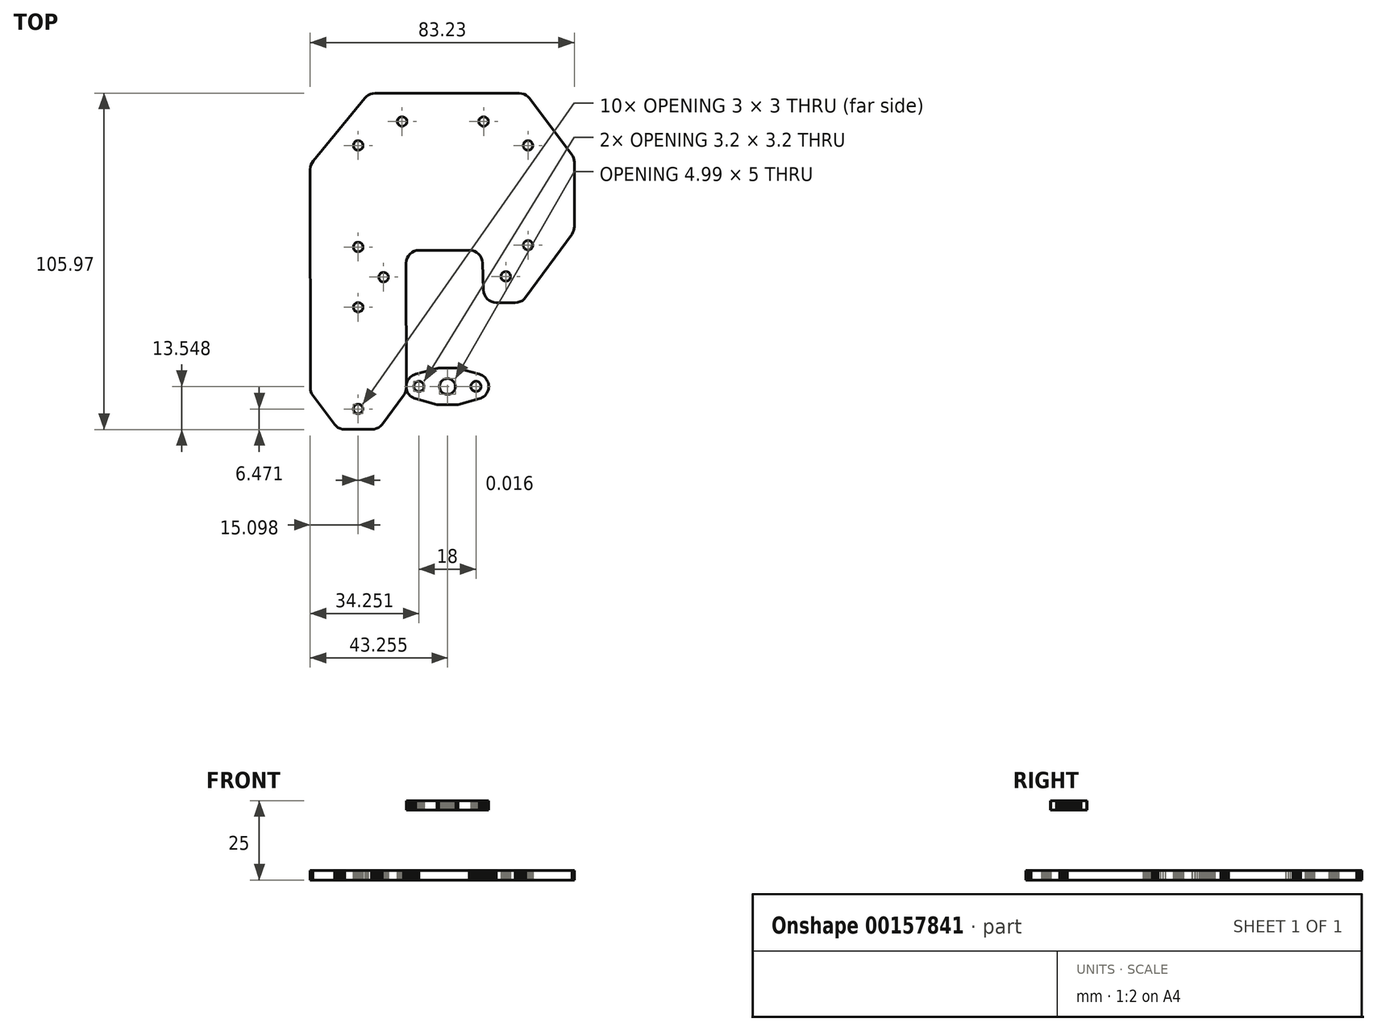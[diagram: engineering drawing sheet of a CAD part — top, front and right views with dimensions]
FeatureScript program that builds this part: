
annotation { "Feature Type Name" : "Feature", "Feature Type Description" : "" }
export const myFeature = defineFeature(function(context is Context, id is Id, definition is map)
    precondition{}
    {
        {
            var Q0;
            Q0=qCreatedBy(makeId("Top.planeOp"),FACE);
            var sketch = newSketch(context, id + "F0", { "sketchPlane" : qUnion([Q0])});
            skLineSegment(sketch, "E0", {"start": v(-52.7, 32.97) * mm, "end": v(-52.37, 33.65) * mm});
            skLineSegment(sketch, "E1", {"start": v(-52.91, 32.24) * mm, "end": v(-52.7, 32.97) * mm});
            skLineSegment(sketch, "E2", {"start": v(-52.98, 31.49) * mm, "end": v(-52.91, 32.24) * mm});
            skLineSegment(sketch, "E3", {"start": v(-52.98, -14.02) * mm, "end": v(-52.98, 31.49) * mm});
            skLineSegment(sketch, "E4", {"start": v(-52.92, -14.74) * mm, "end": v(-52.98, -14.02) * mm});
            skLineSegment(sketch, "E5", {"start": v(-52.73, -15.44) * mm, "end": v(-52.92, -14.74) * mm});
            skLineSegment(sketch, "E6", {"start": v(-52.42, -16.1) * mm, "end": v(-52.73, -15.44) * mm});
            skLineSegment(sketch, "E7", {"start": v(-52, -16.68) * mm, "end": v(-52.42, -16.1) * mm});
            skLineSegment(sketch, "E8", {"start": v(-51.48, -17.19) * mm, "end": v(-52, -16.68) * mm});
            skLineSegment(sketch, "E9", {"start": v(-31.6, -33.48) * mm, "end": v(-51.48, -17.19) * mm});
            skLineSegment(sketch, "E10", {"start": v(-31.03, -33.88) * mm, "end": v(-31.6, -33.48) * mm});
            skLineSegment(sketch, "E11", {"start": v(-30.39, -34.17) * mm, "end": v(-31.03, -33.88) * mm});
            skLineSegment(sketch, "E12", {"start": v(-29.7, -34.35) * mm, "end": v(-30.39, -34.17) * mm});
            skLineSegment(sketch, "E13", {"start": v(-29, -34.4) * mm, "end": v(-29.7, -34.35) * mm});
            skLineSegment(sketch, "E14", {"start": v(39.83, -34.37) * mm, "end": v(-29, -34.4) * mm});
            skLineSegment(sketch, "E15", {"start": v(40.48, -34.32) * mm, "end": v(39.83, -34.37) * mm});
            skLineSegment(sketch, "E16", {"start": v(41.12, -34.16) * mm, "end": v(40.48, -34.32) * mm});
            skLineSegment(sketch, "E17", {"start": v(41.73, -33.9) * mm, "end": v(41.12, -34.16) * mm});
            skLineSegment(sketch, "E18", {"start": v(42.28, -33.55) * mm, "end": v(41.73, -33.9) * mm});
            skLineSegment(sketch, "E19", {"start": v(51.35, -26.76) * mm, "end": v(42.28, -33.55) * mm});
            skLineSegment(sketch, "E20", {"start": v(51.9, -26.25) * mm, "end": v(51.35, -26.76) * mm});
            skLineSegment(sketch, "E21", {"start": v(52.37, -25.64) * mm, "end": v(51.9, -26.25) * mm});
            skLineSegment(sketch, "E22", {"start": v(52.7, -24.96) * mm, "end": v(52.37, -25.64) * mm});
            skLineSegment(sketch, "E23", {"start": v(52.91, -24.23) * mm, "end": v(52.7, -24.96) * mm});
            skLineSegment(sketch, "E24", {"start": v(52.98, -23.48) * mm, "end": v(52.91, -24.23) * mm});
            skLineSegment(sketch, "E25", {"start": v(52.98, -15.05) * mm, "end": v(52.98, -23.48) * mm});
            skLineSegment(sketch, "E26", {"start": v(52.9, -14.3) * mm, "end": v(52.98, -15.05) * mm});
            skLineSegment(sketch, "E27", {"start": v(52.7, -13.56) * mm, "end": v(52.9, -14.3) * mm});
            skLineSegment(sketch, "E28", {"start": v(52.36, -12.89) * mm, "end": v(52.7, -13.56) * mm});
            skLineSegment(sketch, "E29", {"start": v(51.9, -12.28) * mm, "end": v(52.36, -12.89) * mm});
            skLineSegment(sketch, "E30", {"start": v(51.34, -11.77) * mm, "end": v(51.9, -12.28) * mm});
            skLineSegment(sketch, "E31", {"start": v(42.28, -4.98) * mm, "end": v(51.34, -11.77) * mm});
            skLineSegment(sketch, "E32", {"start": v(41.72, -4.63) * mm, "end": v(42.28, -4.98) * mm});
            skLineSegment(sketch, "E33", {"start": v(41.11, -4.37) * mm, "end": v(41.72, -4.63) * mm});
            skLineSegment(sketch, "E34", {"start": v(40.47, -4.21) * mm, "end": v(41.11, -4.37) * mm});
            skLineSegment(sketch, "E35", {"start": v(39.82, -4.16) * mm, "end": v(40.47, -4.21) * mm});
            skLineSegment(sketch, "E36", {"start": v(0.57, -4.2) * mm, "end": v(39.82, -4.16) * mm});
            skLineSegment(sketch, "E37", {"start": v(-0.23, -4.11) * mm, "end": v(0.57, -4.2) * mm});
            skLineSegment(sketch, "E38", {"start": v(-1, -3.88) * mm, "end": v(-0.23, -4.11) * mm});
            skLineSegment(sketch, "E39", {"start": v(-1.7, -3.5) * mm, "end": v(-1, -3.88) * mm});
            skLineSegment(sketch, "E40", {"start": v(-2.33, -3) * mm, "end": v(-1.7, -3.5) * mm});
            skLineSegment(sketch, "E41", {"start": v(-2.84, -2.37) * mm, "end": v(-2.33, -3) * mm});
            skLineSegment(sketch, "E42", {"start": v(-3.22, -1.66) * mm, "end": v(-2.84, -2.37) * mm});
            skLineSegment(sketch, "E43", {"start": v(-3.45, -0.9) * mm, "end": v(-3.22, -1.66) * mm});
            skLineSegment(sketch, "E44", {"start": v(-3.53, -0.1) * mm, "end": v(-3.45, -0.9) * mm});
            skLineSegment(sketch, "E45", {"start": v(-3.53, 15.77) * mm, "end": v(-3.53, -0.1) * mm});
            skLineSegment(sketch, "E46", {"start": v(-3.45, 16.55) * mm, "end": v(-3.53, 15.77) * mm});
            skLineSegment(sketch, "E47", {"start": v(-3.23, 17.3) * mm, "end": v(-3.45, 16.55) * mm});
            skLineSegment(sketch, "E48", {"start": v(-2.87, 18) * mm, "end": v(-3.23, 17.3) * mm});
            skLineSegment(sketch, "E49", {"start": v(-2.37, 18.62) * mm, "end": v(-2.87, 18) * mm});
            skLineSegment(sketch, "E50", {"start": v(-1.78, 19.13) * mm, "end": v(-2.37, 18.62) * mm});
            skLineSegment(sketch, "E51", {"start": v(-1.1, 19.52) * mm, "end": v(-1.78, 19.13) * mm});
            skLineSegment(sketch, "E52", {"start": v(-0.34, 19.76) * mm, "end": v(-1.1, 19.52) * mm});
            skLineSegment(sketch, "E53", {"start": v(0.44, 19.86) * mm, "end": v(-0.34, 19.76) * mm});
            skLineSegment(sketch, "E54", {"start": v(9.04, 20.14) * mm, "end": v(0.44, 19.86) * mm});
            skLineSegment(sketch, "E55", {"start": v(9.82, 20.24) * mm, "end": v(9.04, 20.14) * mm});
            skLineSegment(sketch, "E56", {"start": v(10.57, 20.48) * mm, "end": v(9.82, 20.24) * mm});
            skLineSegment(sketch, "E57", {"start": v(11.25, 20.87) * mm, "end": v(10.57, 20.48) * mm});
            skLineSegment(sketch, "E58", {"start": v(11.85, 21.38) * mm, "end": v(11.25, 20.87) * mm});
            skLineSegment(sketch, "E59", {"start": v(12.34, 22) * mm, "end": v(11.85, 21.38) * mm});
            skLineSegment(sketch, "E60", {"start": v(12.7, 22.7) * mm, "end": v(12.34, 22) * mm});
            skLineSegment(sketch, "E61", {"start": v(12.93, 23.45) * mm, "end": v(12.7, 22.7) * mm});
            skLineSegment(sketch, "E62", {"start": v(13, 24.23) * mm, "end": v(12.93, 23.45) * mm});
            skLineSegment(sketch, "E63", {"start": v(13, 30.23) * mm, "end": v(13, 24.23) * mm});
            skLineSegment(sketch, "E64", {"start": v(12.93, 31) * mm, "end": v(13, 30.23) * mm});
            skLineSegment(sketch, "E65", {"start": v(12.72, 31.73) * mm, "end": v(12.93, 31) * mm});
            skLineSegment(sketch, "E66", {"start": v(12.37, 32.42) * mm, "end": v(12.72, 31.73) * mm});
            skLineSegment(sketch, "E67", {"start": v(11.9, 33.03) * mm, "end": v(12.37, 32.42) * mm});
            skLineSegment(sketch, "E68", {"start": v(11.32, 33.54) * mm, "end": v(11.9, 33.03) * mm});
            skLineSegment(sketch, "E69", {"start": v(-8.58, 48.04) * mm, "end": v(11.32, 33.54) * mm});
            skLineSegment(sketch, "E70", {"start": v(-9.13, 48.38) * mm, "end": v(-8.58, 48.04) * mm});
            skLineSegment(sketch, "E71", {"start": v(-9.72, 48.63) * mm, "end": v(-9.13, 48.38) * mm});
            skLineSegment(sketch, "E72", {"start": v(-10.35, 48.78) * mm, "end": v(-9.72, 48.63) * mm});
            skLineSegment(sketch, "E73", {"start": v(-11, 48.83) * mm, "end": v(-10.35, 48.78) * mm});
            skLineSegment(sketch, "E74", {"start": v(-31.23, 48.83) * mm, "end": v(-11, 48.83) * mm});
            skLineSegment(sketch, "E75", {"start": v(-31.88, 48.77) * mm, "end": v(-31.23, 48.83) * mm});
            skLineSegment(sketch, "E76", {"start": v(-32.52, 48.62) * mm, "end": v(-31.88, 48.77) * mm});
            skLineSegment(sketch, "E77", {"start": v(-33.13, 48.36) * mm, "end": v(-32.52, 48.62) * mm});
            skLineSegment(sketch, "E78", {"start": v(-33.68, 48) * mm, "end": v(-33.13, 48.36) * mm});
            skLineSegment(sketch, "E79", {"start": v(-51.35, 34.76) * mm, "end": v(-33.68, 48) * mm});
            skLineSegment(sketch, "E80", {"start": v(-51.9, 34.25) * mm, "end": v(-51.35, 34.76) * mm});
            skLineSegment(sketch, "E81", {"start": v(-52.37, 33.65) * mm, "end": v(-51.9, 34.25) * mm});
            skLineSegment(sketch, "E82", {"start": v(-37.28, -18) * mm, "end": v(-37.6, -18.23) * mm});
            skLineSegment(sketch, "E83", {"start": v(-36.92, -17.84) * mm, "end": v(-37.28, -18) * mm});
            skLineSegment(sketch, "E84", {"start": v(-36.53, -17.8) * mm, "end": v(-36.92, -17.84) * mm});
            skLineSegment(sketch, "E85", {"start": v(-36.14, -17.84) * mm, "end": v(-36.53, -17.8) * mm});
            skLineSegment(sketch, "E86", {"start": v(-35.78, -18) * mm, "end": v(-36.14, -17.84) * mm});
            skLineSegment(sketch, "E87", {"start": v(-35.47, -18.23) * mm, "end": v(-35.78, -18) * mm});
            skLineSegment(sketch, "E88", {"start": v(-35.23, -18.54) * mm, "end": v(-35.47, -18.23) * mm});
            skLineSegment(sketch, "E89", {"start": v(-35.08, -18.9) * mm, "end": v(-35.23, -18.54) * mm});
            skLineSegment(sketch, "E90", {"start": v(-35.03, -19.3) * mm, "end": v(-35.08, -18.9) * mm});
            skLineSegment(sketch, "E91", {"start": v(-35.08, -19.68) * mm, "end": v(-35.03, -19.3) * mm});
            skLineSegment(sketch, "E92", {"start": v(-35.23, -20.04) * mm, "end": v(-35.08, -19.68) * mm});
            skLineSegment(sketch, "E93", {"start": v(-35.47, -20.35) * mm, "end": v(-35.23, -20.04) * mm});
            skLineSegment(sketch, "E94", {"start": v(-35.78, -20.6) * mm, "end": v(-35.47, -20.35) * mm});
            skLineSegment(sketch, "E95", {"start": v(-36.14, -20.74) * mm, "end": v(-35.78, -20.6) * mm});
            skLineSegment(sketch, "E96", {"start": v(-36.53, -20.8) * mm, "end": v(-36.14, -20.74) * mm});
            skLineSegment(sketch, "E97", {"start": v(-36.92, -20.74) * mm, "end": v(-36.53, -20.8) * mm});
            skLineSegment(sketch, "E98", {"start": v(-37.28, -20.6) * mm, "end": v(-36.92, -20.74) * mm});
            skLineSegment(sketch, "E99", {"start": v(-37.6, -20.35) * mm, "end": v(-37.28, -20.6) * mm});
            skLineSegment(sketch, "E100", {"start": v(-37.83, -20.04) * mm, "end": v(-37.6, -20.35) * mm});
            skLineSegment(sketch, "E101", {"start": v(-37.98, -19.68) * mm, "end": v(-37.83, -20.04) * mm});
            skLineSegment(sketch, "E102", {"start": v(-38.03, -19.3) * mm, "end": v(-37.98, -19.68) * mm});
            skLineSegment(sketch, "E103", {"start": v(-37.98, -18.9) * mm, "end": v(-38.03, -19.3) * mm});
            skLineSegment(sketch, "E104", {"start": v(-37.83, -18.54) * mm, "end": v(-37.98, -18.9) * mm});
            skLineSegment(sketch, "E105", {"start": v(-37.6, -18.23) * mm, "end": v(-37.83, -18.54) * mm});
            skLineSegment(sketch, "E106", {"start": v(-43.7, 21.68) * mm, "end": v(-44.09, 21.73) * mm});
            skLineSegment(sketch, "E107", {"start": v(-43.34, 21.53) * mm, "end": v(-43.7, 21.68) * mm});
            skLineSegment(sketch, "E108", {"start": v(-43.03, 21.3) * mm, "end": v(-43.34, 21.53) * mm});
            skLineSegment(sketch, "E109", {"start": v(-42.8, 20.98) * mm, "end": v(-43.03, 21.3) * mm});
            skLineSegment(sketch, "E110", {"start": v(-42.64, 20.62) * mm, "end": v(-42.8, 20.98) * mm});
            skLineSegment(sketch, "E111", {"start": v(-42.59, 20.23) * mm, "end": v(-42.64, 20.62) * mm});
            skLineSegment(sketch, "E112", {"start": v(-42.64, 19.84) * mm, "end": v(-42.59, 20.23) * mm});
            skLineSegment(sketch, "E113", {"start": v(-42.8, 19.48) * mm, "end": v(-42.64, 19.84) * mm});
            skLineSegment(sketch, "E114", {"start": v(-43.03, 19.17) * mm, "end": v(-42.8, 19.48) * mm});
            skLineSegment(sketch, "E115", {"start": v(-43.34, 18.93) * mm, "end": v(-43.03, 19.17) * mm});
            skLineSegment(sketch, "E116", {"start": v(-43.7, 18.78) * mm, "end": v(-43.34, 18.93) * mm});
            skLineSegment(sketch, "E117", {"start": v(-44.09, 18.73) * mm, "end": v(-43.7, 18.78) * mm});
            skLineSegment(sketch, "E118", {"start": v(-44.48, 18.78) * mm, "end": v(-44.09, 18.73) * mm});
            skLineSegment(sketch, "E119", {"start": v(-44.84, 18.93) * mm, "end": v(-44.48, 18.78) * mm});
            skLineSegment(sketch, "E120", {"start": v(-45.15, 19.17) * mm, "end": v(-44.84, 18.93) * mm});
            skLineSegment(sketch, "E121", {"start": v(-45.39, 19.48) * mm, "end": v(-45.15, 19.17) * mm});
            skLineSegment(sketch, "E122", {"start": v(-45.54, 19.84) * mm, "end": v(-45.39, 19.48) * mm});
            skLineSegment(sketch, "E123", {"start": v(-45.59, 20.23) * mm, "end": v(-45.54, 19.84) * mm});
            skLineSegment(sketch, "E124", {"start": v(-45.54, 20.62) * mm, "end": v(-45.59, 20.23) * mm});
            skLineSegment(sketch, "E125", {"start": v(-45.39, 20.98) * mm, "end": v(-45.54, 20.62) * mm});
            skLineSegment(sketch, "E126", {"start": v(-45.15, 21.3) * mm, "end": v(-45.39, 20.98) * mm});
            skLineSegment(sketch, "E127", {"start": v(-44.84, 21.53) * mm, "end": v(-45.15, 21.3) * mm});
            skLineSegment(sketch, "E128", {"start": v(-44.48, 21.68) * mm, "end": v(-44.84, 21.53) * mm});
            skLineSegment(sketch, "E129", {"start": v(-44.09, 21.73) * mm, "end": v(-44.48, 21.68) * mm});
            skLineSegment(sketch, "E130", {"start": v(-44.09, -6.96) * mm, "end": v(-43.7, -6.9) * mm});
            skLineSegment(sketch, "E131", {"start": v(-44.48, -6.9) * mm, "end": v(-44.09, -6.96) * mm});
            skLineSegment(sketch, "E132", {"start": v(-44.84, -6.76) * mm, "end": v(-44.48, -6.9) * mm});
            skLineSegment(sketch, "E133", {"start": v(-45.15, -6.52) * mm, "end": v(-44.84, -6.76) * mm});
            skLineSegment(sketch, "E134", {"start": v(-45.39, -6.21) * mm, "end": v(-45.15, -6.52) * mm});
            skLineSegment(sketch, "E135", {"start": v(-45.54, -5.85) * mm, "end": v(-45.39, -6.21) * mm});
            skLineSegment(sketch, "E136", {"start": v(-45.59, -5.46) * mm, "end": v(-45.54, -5.85) * mm});
            skLineSegment(sketch, "E137", {"start": v(-45.54, -5.07) * mm, "end": v(-45.59, -5.46) * mm});
            skLineSegment(sketch, "E138", {"start": v(-45.39, -4.71) * mm, "end": v(-45.54, -5.07) * mm});
            skLineSegment(sketch, "E139", {"start": v(-45.15, -4.4) * mm, "end": v(-45.39, -4.71) * mm});
            skLineSegment(sketch, "E140", {"start": v(-44.84, -4.16) * mm, "end": v(-45.15, -4.4) * mm});
            skLineSegment(sketch, "E141", {"start": v(-44.48, -4.01) * mm, "end": v(-44.84, -4.16) * mm});
            skLineSegment(sketch, "E142", {"start": v(-44.09, -3.96) * mm, "end": v(-44.48, -4.01) * mm});
            skLineSegment(sketch, "E143", {"start": v(-43.7, -4.01) * mm, "end": v(-44.09, -3.96) * mm});
            skLineSegment(sketch, "E144", {"start": v(-43.34, -4.16) * mm, "end": v(-43.7, -4.01) * mm});
            skLineSegment(sketch, "E145", {"start": v(-43.03, -4.4) * mm, "end": v(-43.34, -4.16) * mm});
            skLineSegment(sketch, "E146", {"start": v(-42.8, -4.71) * mm, "end": v(-43.03, -4.4) * mm});
            skLineSegment(sketch, "E147", {"start": v(-42.64, -5.07) * mm, "end": v(-42.8, -4.71) * mm});
            skLineSegment(sketch, "E148", {"start": v(-42.59, -5.46) * mm, "end": v(-42.64, -5.07) * mm});
            skLineSegment(sketch, "E149", {"start": v(-42.64, -5.85) * mm, "end": v(-42.59, -5.46) * mm});
            skLineSegment(sketch, "E150", {"start": v(-42.8, -6.21) * mm, "end": v(-42.64, -5.85) * mm});
            skLineSegment(sketch, "E151", {"start": v(-43.03, -6.52) * mm, "end": v(-42.8, -6.21) * mm});
            skLineSegment(sketch, "E152", {"start": v(-43.34, -6.76) * mm, "end": v(-43.03, -6.52) * mm});
            skLineSegment(sketch, "E153", {"start": v(-43.7, -6.9) * mm, "end": v(-43.34, -6.76) * mm});
            skLineSegment(sketch, "E154", {"start": v(-35.47, 33.17) * mm, "end": v(-35.23, 33.48) * mm});
            skLineSegment(sketch, "E155", {"start": v(-35.78, 32.93) * mm, "end": v(-35.47, 33.17) * mm});
            skLineSegment(sketch, "E156", {"start": v(-36.14, 32.78) * mm, "end": v(-35.78, 32.93) * mm});
            skLineSegment(sketch, "E157", {"start": v(-36.53, 32.73) * mm, "end": v(-36.14, 32.78) * mm});
            skLineSegment(sketch, "E158", {"start": v(-36.92, 32.78) * mm, "end": v(-36.53, 32.73) * mm});
            skLineSegment(sketch, "E159", {"start": v(-37.28, 32.93) * mm, "end": v(-36.92, 32.78) * mm});
            skLineSegment(sketch, "E160", {"start": v(-37.6, 33.17) * mm, "end": v(-37.28, 32.93) * mm});
            skLineSegment(sketch, "E161", {"start": v(-37.83, 33.48) * mm, "end": v(-37.6, 33.17) * mm});
            skLineSegment(sketch, "E162", {"start": v(-37.98, 33.84) * mm, "end": v(-37.83, 33.48) * mm});
            skLineSegment(sketch, "E163", {"start": v(-38.03, 34.23) * mm, "end": v(-37.98, 33.84) * mm});
            skLineSegment(sketch, "E164", {"start": v(-37.98, 34.62) * mm, "end": v(-38.03, 34.23) * mm});
            skLineSegment(sketch, "E165", {"start": v(-37.83, 34.98) * mm, "end": v(-37.98, 34.62) * mm});
            skLineSegment(sketch, "E166", {"start": v(-37.6, 35.3) * mm, "end": v(-37.83, 34.98) * mm});
            skLineSegment(sketch, "E167", {"start": v(-37.28, 35.53) * mm, "end": v(-37.6, 35.3) * mm});
            skLineSegment(sketch, "E168", {"start": v(-36.92, 35.68) * mm, "end": v(-37.28, 35.53) * mm});
            skLineSegment(sketch, "E169", {"start": v(-36.53, 35.73) * mm, "end": v(-36.92, 35.68) * mm});
            skLineSegment(sketch, "E170", {"start": v(-36.14, 35.68) * mm, "end": v(-36.53, 35.73) * mm});
            skLineSegment(sketch, "E171", {"start": v(-35.78, 35.53) * mm, "end": v(-36.14, 35.68) * mm});
            skLineSegment(sketch, "E172", {"start": v(-35.47, 35.3) * mm, "end": v(-35.78, 35.53) * mm});
            skLineSegment(sketch, "E173", {"start": v(-35.23, 34.98) * mm, "end": v(-35.47, 35.3) * mm});
            skLineSegment(sketch, "E174", {"start": v(-35.08, 34.62) * mm, "end": v(-35.23, 34.98) * mm});
            skLineSegment(sketch, "E175", {"start": v(-35.03, 34.23) * mm, "end": v(-35.08, 34.62) * mm});
            skLineSegment(sketch, "E176", {"start": v(-35.08, 33.84) * mm, "end": v(-35.03, 34.23) * mm});
            skLineSegment(sketch, "E177", {"start": v(-35.23, 33.48) * mm, "end": v(-35.08, 33.84) * mm});
            skLineSegment(sketch, "E178", {"start": v(-5.09, 32.73) * mm, "end": v(-4.7, 32.78) * mm});
            skLineSegment(sketch, "E179", {"start": v(-5.48, 32.78) * mm, "end": v(-5.09, 32.73) * mm});
            skLineSegment(sketch, "E180", {"start": v(-5.84, 32.93) * mm, "end": v(-5.48, 32.78) * mm});
            skLineSegment(sketch, "E181", {"start": v(-6.15, 33.17) * mm, "end": v(-5.84, 32.93) * mm});
            skLineSegment(sketch, "E182", {"start": v(-6.39, 33.48) * mm, "end": v(-6.15, 33.17) * mm});
            skLineSegment(sketch, "E183", {"start": v(-6.54, 33.84) * mm, "end": v(-6.39, 33.48) * mm});
            skLineSegment(sketch, "E184", {"start": v(-6.59, 34.23) * mm, "end": v(-6.54, 33.84) * mm});
            skLineSegment(sketch, "E185", {"start": v(-6.54, 34.62) * mm, "end": v(-6.59, 34.23) * mm});
            skLineSegment(sketch, "E186", {"start": v(-6.39, 34.98) * mm, "end": v(-6.54, 34.62) * mm});
            skLineSegment(sketch, "E187", {"start": v(-6.15, 35.3) * mm, "end": v(-6.39, 34.98) * mm});
            skLineSegment(sketch, "E188", {"start": v(-5.84, 35.53) * mm, "end": v(-6.15, 35.3) * mm});
            skLineSegment(sketch, "E189", {"start": v(-5.48, 35.68) * mm, "end": v(-5.84, 35.53) * mm});
            skLineSegment(sketch, "E190", {"start": v(-5.09, 35.73) * mm, "end": v(-5.48, 35.68) * mm});
            skLineSegment(sketch, "E191", {"start": v(-4.7, 35.68) * mm, "end": v(-5.09, 35.73) * mm});
            skLineSegment(sketch, "E192", {"start": v(-4.34, 35.53) * mm, "end": v(-4.7, 35.68) * mm});
            skLineSegment(sketch, "E193", {"start": v(-4.03, 35.3) * mm, "end": v(-4.34, 35.53) * mm});
            skLineSegment(sketch, "E194", {"start": v(-3.8, 34.98) * mm, "end": v(-4.03, 35.3) * mm});
            skLineSegment(sketch, "E195", {"start": v(-3.64, 34.62) * mm, "end": v(-3.8, 34.98) * mm});
            skLineSegment(sketch, "E196", {"start": v(-3.59, 34.23) * mm, "end": v(-3.64, 34.62) * mm});
            skLineSegment(sketch, "E197", {"start": v(-3.64, 33.84) * mm, "end": v(-3.59, 34.23) * mm});
            skLineSegment(sketch, "E198", {"start": v(-3.8, 33.48) * mm, "end": v(-3.64, 33.84) * mm});
            skLineSegment(sketch, "E199", {"start": v(-4.03, 33.17) * mm, "end": v(-3.8, 33.48) * mm});
            skLineSegment(sketch, "E200", {"start": v(-4.34, 32.93) * mm, "end": v(-4.03, 33.17) * mm});
            skLineSegment(sketch, "E201", {"start": v(-4.7, 32.78) * mm, "end": v(-4.34, 32.93) * mm});
            skLineSegment(sketch, "E202", {"start": v(4.74, 25.73) * mm, "end": v(5.13, 25.78) * mm});
            skLineSegment(sketch, "E203", {"start": v(4.35, 25.78) * mm, "end": v(4.74, 25.73) * mm});
            skLineSegment(sketch, "E204", {"start": v(3.99, 25.93) * mm, "end": v(4.35, 25.78) * mm});
            skLineSegment(sketch, "E205", {"start": v(3.68, 26.17) * mm, "end": v(3.99, 25.93) * mm});
            skLineSegment(sketch, "E206", {"start": v(3.44, 26.48) * mm, "end": v(3.68, 26.17) * mm});
            skLineSegment(sketch, "E207", {"start": v(3.29, 26.84) * mm, "end": v(3.44, 26.48) * mm});
            skLineSegment(sketch, "E208", {"start": v(3.24, 27.23) * mm, "end": v(3.29, 26.84) * mm});
            skLineSegment(sketch, "E209", {"start": v(3.29, 27.62) * mm, "end": v(3.24, 27.23) * mm});
            skLineSegment(sketch, "E210", {"start": v(3.44, 27.98) * mm, "end": v(3.29, 27.62) * mm});
            skLineSegment(sketch, "E211", {"start": v(3.68, 28.3) * mm, "end": v(3.44, 27.98) * mm});
            skLineSegment(sketch, "E212", {"start": v(3.99, 28.53) * mm, "end": v(3.68, 28.3) * mm});
            skLineSegment(sketch, "E213", {"start": v(4.35, 28.68) * mm, "end": v(3.99, 28.53) * mm});
            skLineSegment(sketch, "E214", {"start": v(4.74, 28.73) * mm, "end": v(4.35, 28.68) * mm});
            skLineSegment(sketch, "E215", {"start": v(5.13, 28.68) * mm, "end": v(4.74, 28.73) * mm});
            skLineSegment(sketch, "E216", {"start": v(5.49, 28.53) * mm, "end": v(5.13, 28.68) * mm});
            skLineSegment(sketch, "E217", {"start": v(5.8, 28.3) * mm, "end": v(5.49, 28.53) * mm});
            skLineSegment(sketch, "E218", {"start": v(6.04, 27.98) * mm, "end": v(5.8, 28.3) * mm});
            skLineSegment(sketch, "E219", {"start": v(6.19, 27.62) * mm, "end": v(6.04, 27.98) * mm});
            skLineSegment(sketch, "E220", {"start": v(6.24, 27.23) * mm, "end": v(6.19, 27.62) * mm});
            skLineSegment(sketch, "E221", {"start": v(6.19, 26.84) * mm, "end": v(6.24, 27.23) * mm});
            skLineSegment(sketch, "E222", {"start": v(6.04, 26.48) * mm, "end": v(6.19, 26.84) * mm});
            skLineSegment(sketch, "E223", {"start": v(5.8, 26.17) * mm, "end": v(6.04, 26.48) * mm});
            skLineSegment(sketch, "E224", {"start": v(5.49, 25.93) * mm, "end": v(5.8, 26.17) * mm});
            skLineSegment(sketch, "E225", {"start": v(5.13, 25.78) * mm, "end": v(5.49, 25.93) * mm});
            skLineSegment(sketch, "E226", {"start": v(3.53, -10.9) * mm, "end": v(3.47, -11.29) * mm});
            skLineSegment(sketch, "E227", {"start": v(3.68, -10.54) * mm, "end": v(3.53, -10.9) * mm});
            skLineSegment(sketch, "E228", {"start": v(3.91, -10.23) * mm, "end": v(3.68, -10.54) * mm});
            skLineSegment(sketch, "E229", {"start": v(4.22, -9.99) * mm, "end": v(3.91, -10.23) * mm});
            skLineSegment(sketch, "E230", {"start": v(4.59, -9.84) * mm, "end": v(4.22, -9.99) * mm});
            skLineSegment(sketch, "E231", {"start": v(4.97, -9.79) * mm, "end": v(4.59, -9.84) * mm});
            skLineSegment(sketch, "E232", {"start": v(5.36, -9.84) * mm, "end": v(4.97, -9.79) * mm});
            skLineSegment(sketch, "E233", {"start": v(5.72, -9.99) * mm, "end": v(5.36, -9.84) * mm});
            skLineSegment(sketch, "E234", {"start": v(6.04, -10.23) * mm, "end": v(5.72, -9.99) * mm});
            skLineSegment(sketch, "E235", {"start": v(6.27, -10.54) * mm, "end": v(6.04, -10.23) * mm});
            skLineSegment(sketch, "E236", {"start": v(6.42, -10.9) * mm, "end": v(6.27, -10.54) * mm});
            skLineSegment(sketch, "E237", {"start": v(6.47, -11.29) * mm, "end": v(6.42, -10.9) * mm});
            skLineSegment(sketch, "E238", {"start": v(6.42, -11.68) * mm, "end": v(6.47, -11.29) * mm});
            skLineSegment(sketch, "E239", {"start": v(6.27, -12.04) * mm, "end": v(6.42, -11.68) * mm});
            skLineSegment(sketch, "E240", {"start": v(6.04, -12.35) * mm, "end": v(6.27, -12.04) * mm});
            skLineSegment(sketch, "E241", {"start": v(5.72, -12.59) * mm, "end": v(6.04, -12.35) * mm});
            skLineSegment(sketch, "E242", {"start": v(5.36, -12.74) * mm, "end": v(5.72, -12.59) * mm});
            skLineSegment(sketch, "E243", {"start": v(4.97, -12.79) * mm, "end": v(5.36, -12.74) * mm});
            skLineSegment(sketch, "E244", {"start": v(4.59, -12.74) * mm, "end": v(4.97, -12.79) * mm});
            skLineSegment(sketch, "E245", {"start": v(4.22, -12.59) * mm, "end": v(4.59, -12.74) * mm});
            skLineSegment(sketch, "E246", {"start": v(3.91, -12.35) * mm, "end": v(4.22, -12.59) * mm});
            skLineSegment(sketch, "E247", {"start": v(3.68, -12.04) * mm, "end": v(3.91, -12.35) * mm});
            skLineSegment(sketch, "E248", {"start": v(3.53, -11.68) * mm, "end": v(3.68, -12.04) * mm});
            skLineSegment(sketch, "E249", {"start": v(3.47, -11.29) * mm, "end": v(3.53, -11.68) * mm});
            skLineSegment(sketch, "E250", {"start": v(-4.91, -20.74) * mm, "end": v(-4.53, -20.8) * mm});
            skLineSegment(sketch, "E251", {"start": v(-5.28, -20.6) * mm, "end": v(-4.91, -20.74) * mm});
            skLineSegment(sketch, "E252", {"start": v(-5.59, -20.35) * mm, "end": v(-5.28, -20.6) * mm});
            skLineSegment(sketch, "E253", {"start": v(-5.82, -20.04) * mm, "end": v(-5.59, -20.35) * mm});
            skLineSegment(sketch, "E254", {"start": v(-5.97, -19.68) * mm, "end": v(-5.82, -20.04) * mm});
            skLineSegment(sketch, "E255", {"start": v(-6.03, -19.3) * mm, "end": v(-5.97, -19.68) * mm});
            skLineSegment(sketch, "E256", {"start": v(-5.97, -18.9) * mm, "end": v(-6.03, -19.3) * mm});
            skLineSegment(sketch, "E257", {"start": v(-5.82, -18.54) * mm, "end": v(-5.97, -18.9) * mm});
            skLineSegment(sketch, "E258", {"start": v(-5.59, -18.23) * mm, "end": v(-5.82, -18.54) * mm});
            skLineSegment(sketch, "E259", {"start": v(-5.28, -18) * mm, "end": v(-5.59, -18.23) * mm});
            skLineSegment(sketch, "E260", {"start": v(-4.91, -17.84) * mm, "end": v(-5.28, -18) * mm});
            skLineSegment(sketch, "E261", {"start": v(-4.53, -17.8) * mm, "end": v(-4.91, -17.84) * mm});
            skLineSegment(sketch, "E262", {"start": v(-4.14, -17.84) * mm, "end": v(-4.53, -17.8) * mm});
            skLineSegment(sketch, "E263", {"start": v(-3.78, -18) * mm, "end": v(-4.14, -17.84) * mm});
            skLineSegment(sketch, "E264", {"start": v(-3.46, -18.23) * mm, "end": v(-3.78, -18) * mm});
            skLineSegment(sketch, "E265", {"start": v(-3.23, -18.54) * mm, "end": v(-3.46, -18.23) * mm});
            skLineSegment(sketch, "E266", {"start": v(-3.08, -18.9) * mm, "end": v(-3.23, -18.54) * mm});
            skLineSegment(sketch, "E267", {"start": v(-3.03, -19.3) * mm, "end": v(-3.08, -18.9) * mm});
            skLineSegment(sketch, "E268", {"start": v(-3.08, -19.68) * mm, "end": v(-3.03, -19.3) * mm});
            skLineSegment(sketch, "E269", {"start": v(-3.23, -20.04) * mm, "end": v(-3.08, -19.68) * mm});
            skLineSegment(sketch, "E270", {"start": v(-3.46, -20.35) * mm, "end": v(-3.23, -20.04) * mm});
            skLineSegment(sketch, "E271", {"start": v(-3.78, -20.6) * mm, "end": v(-3.46, -20.35) * mm});
            skLineSegment(sketch, "E272", {"start": v(-4.14, -20.74) * mm, "end": v(-3.78, -20.6) * mm});
            skLineSegment(sketch, "E273", {"start": v(-4.53, -20.8) * mm, "end": v(-4.14, -20.74) * mm});
            skLineSegment(sketch, "E274", {"start": v(15.54, -20.34) * mm, "end": v(15.77, -20.03) * mm});
            skLineSegment(sketch, "E275", {"start": v(15.22, -20.58) * mm, "end": v(15.54, -20.34) * mm});
            skLineSegment(sketch, "E276", {"start": v(14.86, -20.73) * mm, "end": v(15.22, -20.58) * mm});
            skLineSegment(sketch, "E277", {"start": v(14.47, -20.78) * mm, "end": v(14.86, -20.73) * mm});
            skLineSegment(sketch, "E278", {"start": v(14.09, -20.73) * mm, "end": v(14.47, -20.78) * mm});
            skLineSegment(sketch, "E279", {"start": v(13.72, -20.58) * mm, "end": v(14.09, -20.73) * mm});
            skLineSegment(sketch, "E280", {"start": v(13.41, -20.34) * mm, "end": v(13.72, -20.58) * mm});
            skLineSegment(sketch, "E281", {"start": v(13.18, -20.03) * mm, "end": v(13.41, -20.34) * mm});
            skLineSegment(sketch, "E282", {"start": v(13.03, -19.67) * mm, "end": v(13.18, -20.03) * mm});
            skLineSegment(sketch, "E283", {"start": v(12.97, -19.28) * mm, "end": v(13.03, -19.67) * mm});
            skLineSegment(sketch, "E284", {"start": v(13.03, -18.9) * mm, "end": v(12.97, -19.28) * mm});
            skLineSegment(sketch, "E285", {"start": v(13.18, -18.53) * mm, "end": v(13.03, -18.9) * mm});
            skLineSegment(sketch, "E286", {"start": v(13.41, -18.22) * mm, "end": v(13.18, -18.53) * mm});
            skLineSegment(sketch, "E287", {"start": v(13.72, -17.98) * mm, "end": v(13.41, -18.22) * mm});
            skLineSegment(sketch, "E288", {"start": v(14.09, -17.83) * mm, "end": v(13.72, -17.98) * mm});
            skLineSegment(sketch, "E289", {"start": v(14.47, -17.78) * mm, "end": v(14.09, -17.83) * mm});
            skLineSegment(sketch, "E290", {"start": v(14.86, -17.83) * mm, "end": v(14.47, -17.78) * mm});
            skLineSegment(sketch, "E291", {"start": v(15.22, -17.98) * mm, "end": v(14.86, -17.83) * mm});
            skLineSegment(sketch, "E292", {"start": v(15.54, -18.22) * mm, "end": v(15.22, -17.98) * mm});
            skLineSegment(sketch, "E293", {"start": v(15.77, -18.53) * mm, "end": v(15.54, -18.22) * mm});
            skLineSegment(sketch, "E294", {"start": v(15.92, -18.9) * mm, "end": v(15.77, -18.53) * mm});
            skLineSegment(sketch, "E295", {"start": v(15.97, -19.28) * mm, "end": v(15.92, -18.9) * mm});
            skLineSegment(sketch, "E296", {"start": v(15.92, -19.67) * mm, "end": v(15.97, -19.28) * mm});
            skLineSegment(sketch, "E297", {"start": v(15.77, -20.03) * mm, "end": v(15.92, -19.67) * mm});
            skLineSegment(sketch, "E298", {"start": v(46.13, -20.76) * mm, "end": v(46.51, -20.8) * mm});
            skLineSegment(sketch, "E299", {"start": v(45.76, -20.6) * mm, "end": v(46.13, -20.76) * mm});
            skLineSegment(sketch, "E300", {"start": v(45.45, -20.37) * mm, "end": v(45.76, -20.6) * mm});
            skLineSegment(sketch, "E301", {"start": v(45.22, -20.06) * mm, "end": v(45.45, -20.37) * mm});
            skLineSegment(sketch, "E302", {"start": v(45.07, -19.7) * mm, "end": v(45.22, -20.06) * mm});
            skLineSegment(sketch, "E303", {"start": v(45.01, -19.3) * mm, "end": v(45.07, -19.7) * mm});
            skLineSegment(sketch, "E304", {"start": v(45.07, -18.92) * mm, "end": v(45.01, -19.3) * mm});
            skLineSegment(sketch, "E305", {"start": v(45.22, -18.56) * mm, "end": v(45.07, -18.92) * mm});
            skLineSegment(sketch, "E306", {"start": v(45.45, -18.25) * mm, "end": v(45.22, -18.56) * mm});
            skLineSegment(sketch, "E307", {"start": v(45.76, -18) * mm, "end": v(45.45, -18.25) * mm});
            skLineSegment(sketch, "E308", {"start": v(46.13, -17.86) * mm, "end": v(45.76, -18) * mm});
            skLineSegment(sketch, "E309", {"start": v(46.51, -17.8) * mm, "end": v(46.13, -17.86) * mm});
            skLineSegment(sketch, "E310", {"start": v(46.9, -17.86) * mm, "end": v(46.51, -17.8) * mm});
            skLineSegment(sketch, "E311", {"start": v(47.26, -18) * mm, "end": v(46.9, -17.86) * mm});
            skLineSegment(sketch, "E312", {"start": v(47.58, -18.25) * mm, "end": v(47.26, -18) * mm});
            skLineSegment(sketch, "E313", {"start": v(47.81, -18.56) * mm, "end": v(47.58, -18.25) * mm});
            skLineSegment(sketch, "E314", {"start": v(47.96, -18.92) * mm, "end": v(47.81, -18.56) * mm});
            skLineSegment(sketch, "E315", {"start": v(48.01, -19.3) * mm, "end": v(47.96, -18.92) * mm});
            skLineSegment(sketch, "E316", {"start": v(47.96, -19.7) * mm, "end": v(48.01, -19.3) * mm});
            skLineSegment(sketch, "E317", {"start": v(47.81, -20.06) * mm, "end": v(47.96, -19.7) * mm});
            skLineSegment(sketch, "E318", {"start": v(47.58, -20.37) * mm, "end": v(47.81, -20.06) * mm});
            skLineSegment(sketch, "E319", {"start": v(47.26, -20.6) * mm, "end": v(47.58, -20.37) * mm});
            skLineSegment(sketch, "E320", {"start": v(46.9, -20.76) * mm, "end": v(47.26, -20.6) * mm});
            skLineSegment(sketch, "E321", {"start": v(46.51, -20.8) * mm, "end": v(46.9, -20.76) * mm});
            skLineSegment(sketch, "E322", {"start": v(-5.97, -46.28) * mm, "end": v(-6.35, -45.96) * mm});
            skLineSegment(sketch, "E323", {"start": v(-4.63, -46.92) * mm, "end": v(-5.1, -46.76) * mm});
            skLineSegment(sketch, "E324", {"start": v(-7.52, -42.32) * mm, "end": v(-7.4, -41.84) * mm});
            skLineSegment(sketch, "E325", {"start": v(-7.4, -41.84) * mm, "end": v(-7.22, -41.37) * mm});
            skLineSegment(sketch, "E326", {"start": v(-6.69, -40.53) * mm, "end": v(-6.35, -40.17) * mm});
            skLineSegment(sketch, "E327", {"start": v(-4.63, -46.92) * mm, "end": v(2.15, -48.76) * mm});
            skLineSegment(sketch, "E328", {"start": v(-5.97, -39.85) * mm, "end": v(-5.55, -39.58) * mm});
            skLineSegment(sketch, "E329", {"start": v(-5.1, -39.36) * mm, "end": v(-4.63, -39.2) * mm});
            skLineSegment(sketch, "E330", {"start": v(-4.63, -39.2) * mm, "end": v(2.15, -37.37) * mm});
            skLineSegment(sketch, "E331", {"start": v(-6.35, -45.96) * mm, "end": v(-6.69, -45.6) * mm});
            skLineSegment(sketch, "E332", {"start": v(2.33, -37.33) * mm, "end": v(2.5, -37.3) * mm});
            skLineSegment(sketch, "E333", {"start": v(2.5, -37.3) * mm, "end": v(2.68, -37.3) * mm});
            skLineSegment(sketch, "E334", {"start": v(2.68, -37.3) * mm, "end": v(8.15, -37.3) * mm});
            skLineSegment(sketch, "E335", {"start": v(8.32, -37.3) * mm, "end": v(8.15, -37.3) * mm});
            skLineSegment(sketch, "E336", {"start": v(8.32, -37.3) * mm, "end": v(8.5, -37.33) * mm});
            skLineSegment(sketch, "E337", {"start": v(8.5, -37.33) * mm, "end": v(8.67, -37.37) * mm});
            skLineSegment(sketch, "E338", {"start": v(3.83, -41.13) * mm, "end": v(4.16, -40.9) * mm});
            skLineSegment(sketch, "E339", {"start": v(-7.22, -41.37) * mm, "end": v(-6.98, -40.94) * mm});
            skLineSegment(sketch, "E340", {"start": v(3.54, -41.4) * mm, "end": v(3.83, -41.13) * mm});
            skLineSegment(sketch, "E341", {"start": v(3.3, -41.73) * mm, "end": v(3.54, -41.4) * mm});
            skLineSegment(sketch, "E342", {"start": v(16.8, -46.28) * mm, "end": v(16.37, -46.55) * mm});
            skLineSegment(sketch, "E343", {"start": v(-7.58, -42.81) * mm, "end": v(-7.52, -42.32) * mm});
            skLineSegment(sketch, "E344", {"start": v(-7.58, -43.31) * mm, "end": v(-7.58, -42.81) * mm});
            skLineSegment(sketch, "E345", {"start": v(-5.55, -46.55) * mm, "end": v(-5.97, -46.28) * mm});
            skLineSegment(sketch, "E346", {"start": v(2.5, -48.82) * mm, "end": v(2.68, -48.83) * mm});
            skLineSegment(sketch, "E347", {"start": v(8.32, -48.82) * mm, "end": v(8.5, -48.8) * mm});
            skLineSegment(sketch, "E348", {"start": v(-7.4, -44.29) * mm, "end": v(-7.52, -43.8) * mm});
            skLineSegment(sketch, "E349", {"start": v(-6.98, -40.94) * mm, "end": v(-6.69, -40.53) * mm});
            skLineSegment(sketch, "E350", {"start": v(2.33, -48.8) * mm, "end": v(2.15, -48.76) * mm});
            skLineSegment(sketch, "E351", {"start": v(-6.35, -40.17) * mm, "end": v(-5.97, -39.85) * mm});
            skLineSegment(sketch, "E352", {"start": v(2.5, -48.82) * mm, "end": v(2.33, -48.8) * mm});
            skLineSegment(sketch, "E353", {"start": v(-6.69, -45.6) * mm, "end": v(-6.98, -45.19) * mm});
            skLineSegment(sketch, "E354", {"start": v(-5.55, -39.58) * mm, "end": v(-5.1, -39.36) * mm});
            skLineSegment(sketch, "E355", {"start": v(2.15, -37.37) * mm, "end": v(2.33, -37.33) * mm});
            skLineSegment(sketch, "E356", {"start": v(8.15, -48.83) * mm, "end": v(8.32, -48.82) * mm});
            skLineSegment(sketch, "E357", {"start": v(15.93, -46.76) * mm, "end": v(15.45, -46.92) * mm});
            skLineSegment(sketch, "E358", {"start": v(2.68, -48.83) * mm, "end": v(8.15, -48.83) * mm});
            skLineSegment(sketch, "E359", {"start": v(16.37, -46.55) * mm, "end": v(15.93, -46.76) * mm});
            skLineSegment(sketch, "E360", {"start": v(8.67, -48.76) * mm, "end": v(15.45, -46.92) * mm});
            skLineSegment(sketch, "E361", {"start": v(-5.1, -46.76) * mm, "end": v(-5.55, -46.55) * mm});
            skLineSegment(sketch, "E362", {"start": v(-6.98, -45.19) * mm, "end": v(-7.22, -44.75) * mm});
            skLineSegment(sketch, "E363", {"start": v(-7.22, -44.75) * mm, "end": v(-7.4, -44.29) * mm});
            skLineSegment(sketch, "E364", {"start": v(8.67, -48.76) * mm, "end": v(8.5, -48.8) * mm});
            skLineSegment(sketch, "E365", {"start": v(-7.52, -43.8) * mm, "end": v(-7.58, -43.31) * mm});
            skLineSegment(sketch, "E366", {"start": v(7.62, -44.22) * mm, "end": v(7.4, -44.56) * mm});
            skLineSegment(sketch, "E367", {"start": v(-3.59, -44.66) * mm, "end": v(-3.28, -44.63) * mm});
            skLineSegment(sketch, "E368", {"start": v(5.71, -40.58) * mm, "end": v(6.1, -40.66) * mm});
            skLineSegment(sketch, "E369", {"start": v(3.3, -44.4) * mm, "end": v(3.11, -44.04) * mm});
            skLineSegment(sketch, "E370", {"start": v(4.16, -45.23) * mm, "end": v(3.83, -45) * mm});
            skLineSegment(sketch, "E371", {"start": v(7.78, -42.27) * mm, "end": v(7.88, -42.66) * mm});
            skLineSegment(sketch, "E372", {"start": v(2.98, -43.66) * mm, "end": v(2.92, -43.26) * mm});
            skLineSegment(sketch, "E373", {"start": v(2.92, -42.86) * mm, "end": v(2.98, -42.46) * mm});
            skLineSegment(sketch, "E374", {"start": v(2.92, -43.26) * mm, "end": v(2.92, -42.86) * mm});
            skLineSegment(sketch, "E375", {"start": v(3.11, -42.08) * mm, "end": v(3.3, -41.73) * mm});
            skLineSegment(sketch, "E376", {"start": v(7.88, -42.66) * mm, "end": v(7.91, -43.06) * mm});
            skLineSegment(sketch, "E377", {"start": v(5.71, -45.54) * mm, "end": v(5.31, -45.56) * mm});
            skLineSegment(sketch, "E378", {"start": v(6.83, -41) * mm, "end": v(7.14, -41.26) * mm});
            skLineSegment(sketch, "E379", {"start": v(4.52, -45.4) * mm, "end": v(4.16, -45.23) * mm});
            skLineSegment(sketch, "E380", {"start": v(6.1, -45.46) * mm, "end": v(5.71, -45.54) * mm});
            skLineSegment(sketch, "E381", {"start": v(7.78, -43.85) * mm, "end": v(7.62, -44.22) * mm});
            skLineSegment(sketch, "E382", {"start": v(6.48, -40.8) * mm, "end": v(6.83, -41) * mm});
            skLineSegment(sketch, "E383", {"start": v(6.1, -40.66) * mm, "end": v(6.48, -40.8) * mm});
            skLineSegment(sketch, "E384", {"start": v(6.48, -45.32) * mm, "end": v(6.1, -45.46) * mm});
            skLineSegment(sketch, "E385", {"start": v(5.31, -45.56) * mm, "end": v(4.91, -45.51) * mm});
            skLineSegment(sketch, "E386", {"start": v(7.91, -43.06) * mm, "end": v(7.88, -43.46) * mm});
            skLineSegment(sketch, "E387", {"start": v(7.62, -41.9) * mm, "end": v(7.78, -42.27) * mm});
            skLineSegment(sketch, "E388", {"start": v(7.14, -41.26) * mm, "end": v(7.4, -41.56) * mm});
            skLineSegment(sketch, "E389", {"start": v(5.31, -40.56) * mm, "end": v(5.71, -40.58) * mm});
            skLineSegment(sketch, "E390", {"start": v(7.14, -44.87) * mm, "end": v(6.83, -45.12) * mm});
            skLineSegment(sketch, "E391", {"start": v(4.91, -40.61) * mm, "end": v(5.31, -40.56) * mm});
            skLineSegment(sketch, "E392", {"start": v(4.52, -40.72) * mm, "end": v(4.91, -40.61) * mm});
            skLineSegment(sketch, "E393", {"start": v(4.16, -40.9) * mm, "end": v(4.52, -40.72) * mm});
            skLineSegment(sketch, "E394", {"start": v(7.4, -41.56) * mm, "end": v(7.62, -41.9) * mm});
            skLineSegment(sketch, "E395", {"start": v(7.88, -43.46) * mm, "end": v(7.78, -43.85) * mm});
            skLineSegment(sketch, "E396", {"start": v(-3.28, -44.63) * mm, "end": v(-2.98, -44.54) * mm});
            skLineSegment(sketch, "E397", {"start": v(6.83, -45.12) * mm, "end": v(6.48, -45.32) * mm});
            skLineSegment(sketch, "E398", {"start": v(4.91, -45.51) * mm, "end": v(4.52, -45.4) * mm});
            skLineSegment(sketch, "E399", {"start": v(3.83, -45) * mm, "end": v(3.54, -44.72) * mm});
            skLineSegment(sketch, "E400", {"start": v(2.98, -42.46) * mm, "end": v(3.11, -42.08) * mm});
            skLineSegment(sketch, "E401", {"start": v(7.4, -44.56) * mm, "end": v(7.14, -44.87) * mm});
            skLineSegment(sketch, "E402", {"start": v(3.11, -44.04) * mm, "end": v(2.98, -43.66) * mm});
            skLineSegment(sketch, "E403", {"start": v(3.54, -44.72) * mm, "end": v(3.3, -44.4) * mm});
            skLineSegment(sketch, "E404", {"start": v(-4.48, -41.73) * mm, "end": v(-4.72, -41.93) * mm});
            skLineSegment(sketch, "E405", {"start": v(-5.07, -42.45) * mm, "end": v(-5.16, -42.75) * mm});
            skLineSegment(sketch, "E406", {"start": v(-4.72, -44.2) * mm, "end": v(-4.48, -44.4) * mm});
            skLineSegment(sketch, "E407", {"start": v(14.1, -41.5) * mm, "end": v(13.8, -41.58) * mm});
            skLineSegment(sketch, "E408", {"start": v(-4.2, -44.54) * mm, "end": v(-3.9, -44.63) * mm});
            skLineSegment(sketch, "E409", {"start": v(13.8, -41.58) * mm, "end": v(13.52, -41.73) * mm});
            skLineSegment(sketch, "E410", {"start": v(13.28, -41.93) * mm, "end": v(13.08, -42.17) * mm});
            skLineSegment(sketch, "E411", {"start": v(-2.7, -44.4) * mm, "end": v(-2.46, -44.2) * mm});
            skLineSegment(sketch, "E412", {"start": v(-4.2, -41.58) * mm, "end": v(-4.48, -41.73) * mm});
            skLineSegment(sketch, "E413", {"start": v(-2.26, -42.17) * mm, "end": v(-2.46, -41.93) * mm});
            skLineSegment(sketch, "E414", {"start": v(-5.16, -42.75) * mm, "end": v(-5.19, -43.06) * mm});
            skLineSegment(sketch, "E415", {"start": v(-5.19, -43.06) * mm, "end": v(-5.16, -43.37) * mm});
            skLineSegment(sketch, "E416", {"start": v(-2.46, -44.2) * mm, "end": v(-2.26, -43.95) * mm});
            skLineSegment(sketch, "E417", {"start": v(-5.16, -43.37) * mm, "end": v(-5.07, -43.67) * mm});
            skLineSegment(sketch, "E418", {"start": v(-4.92, -43.95) * mm, "end": v(-4.72, -44.2) * mm});
            skLineSegment(sketch, "E419", {"start": v(-4.48, -44.4) * mm, "end": v(-4.2, -44.54) * mm});
            skLineSegment(sketch, "E420", {"start": v(12.93, -42.45) * mm, "end": v(12.84, -42.75) * mm});
            skLineSegment(sketch, "E421", {"start": v(14.41, -41.46) * mm, "end": v(14.1, -41.5) * mm});
            skLineSegment(sketch, "E422", {"start": v(-2.98, -41.58) * mm, "end": v(-3.28, -41.5) * mm});
            skLineSegment(sketch, "E423", {"start": v(-2.98, -44.54) * mm, "end": v(-2.7, -44.4) * mm});
            skLineSegment(sketch, "E424", {"start": v(-4.92, -42.17) * mm, "end": v(-5.07, -42.45) * mm});
            skLineSegment(sketch, "E425", {"start": v(-5.07, -43.67) * mm, "end": v(-4.92, -43.95) * mm});
            skLineSegment(sketch, "E426", {"start": v(13.52, -41.73) * mm, "end": v(13.28, -41.93) * mm});
            skLineSegment(sketch, "E427", {"start": v(12.84, -42.75) * mm, "end": v(12.81, -43.06) * mm});
            skLineSegment(sketch, "E428", {"start": v(-3.28, -41.5) * mm, "end": v(-3.59, -41.46) * mm});
            skLineSegment(sketch, "E429", {"start": v(-3.59, -41.46) * mm, "end": v(-3.9, -41.5) * mm});
            skLineSegment(sketch, "E430", {"start": v(-2.46, -41.93) * mm, "end": v(-2.7, -41.73) * mm});
            skLineSegment(sketch, "E431", {"start": v(-3.9, -44.63) * mm, "end": v(-3.59, -44.66) * mm});
            skLineSegment(sketch, "E432", {"start": v(13.08, -42.17) * mm, "end": v(12.93, -42.45) * mm});
            skLineSegment(sketch, "E433", {"start": v(-2.26, -43.95) * mm, "end": v(-2.11, -43.67) * mm});
            skLineSegment(sketch, "E434", {"start": v(-4.72, -41.93) * mm, "end": v(-4.92, -42.17) * mm});
            skLineSegment(sketch, "E435", {"start": v(12.81, -43.06) * mm, "end": v(12.84, -43.37) * mm});
            skLineSegment(sketch, "E436", {"start": v(12.84, -43.37) * mm, "end": v(12.93, -43.67) * mm});
            skLineSegment(sketch, "E437", {"start": v(12.93, -43.67) * mm, "end": v(13.08, -43.95) * mm});
            skLineSegment(sketch, "E438", {"start": v(-2.02, -42.75) * mm, "end": v(-2.11, -42.45) * mm});
            skLineSegment(sketch, "E439", {"start": v(-3.9, -41.5) * mm, "end": v(-4.2, -41.58) * mm});
            skLineSegment(sketch, "E440", {"start": v(-2.02, -43.37) * mm, "end": v(-1.99, -43.06) * mm});
            skLineSegment(sketch, "E441", {"start": v(-1.99, -43.06) * mm, "end": v(-2.02, -42.75) * mm});
            skLineSegment(sketch, "E442", {"start": v(-2.11, -42.45) * mm, "end": v(-2.26, -42.17) * mm});
            skLineSegment(sketch, "E443", {"start": v(-2.11, -43.67) * mm, "end": v(-2.02, -43.37) * mm});
            skLineSegment(sketch, "E444", {"start": v(-2.7, -41.73) * mm, "end": v(-2.98, -41.58) * mm});
            skLineSegment(sketch, "E445", {"start": v(15.74, -43.95) * mm, "end": v(15.89, -43.67) * mm});
            skLineSegment(sketch, "E446", {"start": v(13.8, -44.54) * mm, "end": v(14.1, -44.63) * mm});
            skLineSegment(sketch, "E447", {"start": v(13.08, -43.95) * mm, "end": v(13.28, -44.2) * mm});
            skLineSegment(sketch, "E448", {"start": v(15.3, -44.4) * mm, "end": v(15.54, -44.2) * mm});
            skLineSegment(sketch, "E449", {"start": v(15.3, -41.73) * mm, "end": v(15.02, -41.58) * mm});
            skLineSegment(sketch, "E450", {"start": v(13.52, -44.4) * mm, "end": v(13.8, -44.54) * mm});
            skLineSegment(sketch, "E451", {"start": v(15.54, -44.2) * mm, "end": v(15.74, -43.95) * mm});
            skLineSegment(sketch, "E452", {"start": v(15.89, -43.67) * mm, "end": v(15.98, -43.37) * mm});
            skLineSegment(sketch, "E453", {"start": v(15.98, -43.37) * mm, "end": v(16.01, -43.06) * mm});
            skLineSegment(sketch, "E454", {"start": v(15.74, -42.17) * mm, "end": v(15.54, -41.93) * mm});
            skLineSegment(sketch, "E455", {"start": v(15.54, -41.93) * mm, "end": v(15.3, -41.73) * mm});
            skLineSegment(sketch, "E456", {"start": v(14.41, -44.66) * mm, "end": v(14.72, -44.63) * mm});
            skLineSegment(sketch, "E457", {"start": v(15.02, -44.54) * mm, "end": v(15.3, -44.4) * mm});
            skLineSegment(sketch, "E458", {"start": v(13.28, -44.2) * mm, "end": v(13.52, -44.4) * mm});
            skLineSegment(sketch, "E459", {"start": v(15.89, -42.45) * mm, "end": v(15.74, -42.17) * mm});
            skLineSegment(sketch, "E460", {"start": v(14.1, -44.63) * mm, "end": v(14.41, -44.66) * mm});
            skLineSegment(sketch, "E461", {"start": v(14.72, -41.5) * mm, "end": v(14.41, -41.46) * mm});
            skLineSegment(sketch, "E462", {"start": v(14.72, -44.63) * mm, "end": v(15.02, -44.54) * mm});
            skLineSegment(sketch, "E463", {"start": v(15.98, -42.75) * mm, "end": v(15.89, -42.45) * mm});
            skLineSegment(sketch, "E464", {"start": v(15.02, -41.58) * mm, "end": v(14.72, -41.5) * mm});
            skLineSegment(sketch, "E465", {"start": v(16.01, -43.06) * mm, "end": v(15.98, -42.75) * mm});
            skLineSegment(sketch, "E466", {"start": v(8.67, -37.37) * mm, "end": v(15.45, -39.2) * mm});
            skLineSegment(sketch, "E467", {"start": v(15.45, -39.2) * mm, "end": v(15.93, -39.36) * mm});
            skLineSegment(sketch, "E468", {"start": v(15.93, -39.36) * mm, "end": v(16.37, -39.58) * mm});
            skLineSegment(sketch, "E469", {"start": v(16.37, -39.58) * mm, "end": v(16.8, -39.85) * mm});
            skLineSegment(sketch, "E470", {"start": v(16.8, -39.85) * mm, "end": v(17.17, -40.17) * mm});
            skLineSegment(sketch, "E471", {"start": v(17.17, -40.17) * mm, "end": v(17.5, -40.53) * mm});
            skLineSegment(sketch, "E472", {"start": v(17.5, -40.53) * mm, "end": v(17.8, -40.94) * mm});
            skLineSegment(sketch, "E473", {"start": v(17.8, -40.94) * mm, "end": v(18.04, -41.37) * mm});
            skLineSegment(sketch, "E474", {"start": v(18.04, -41.37) * mm, "end": v(18.22, -41.84) * mm});
            skLineSegment(sketch, "E475", {"start": v(18.22, -41.84) * mm, "end": v(18.34, -42.32) * mm});
            skLineSegment(sketch, "E476", {"start": v(18.34, -42.32) * mm, "end": v(18.4, -42.81) * mm});
            skLineSegment(sketch, "E477", {"start": v(18.4, -42.81) * mm, "end": v(18.4, -43.31) * mm});
            skLineSegment(sketch, "E478", {"start": v(18.4, -43.31) * mm, "end": v(18.34, -43.8) * mm});
            skLineSegment(sketch, "E479", {"start": v(18.34, -43.8) * mm, "end": v(18.22, -44.29) * mm});
            skLineSegment(sketch, "E480", {"start": v(18.22, -44.29) * mm, "end": v(18.04, -44.75) * mm});
            skLineSegment(sketch, "E481", {"start": v(18.04, -44.75) * mm, "end": v(17.8, -45.19) * mm});
            skLineSegment(sketch, "E482", {"start": v(17.8, -45.19) * mm, "end": v(17.5, -45.6) * mm});
            skLineSegment(sketch, "E483", {"start": v(17.5, -45.6) * mm, "end": v(17.17, -45.96) * mm});
            skLineSegment(sketch, "E484", {"start": v(17.17, -45.96) * mm, "end": v(16.8, -46.28) * mm});
            skSolve(sketch);
        }
        {
            var Q0;
            Q0=makeQuery(id+"F0.imprint","IMPRINT",FACE,{"disambiguationData":[TD([[makeQuery(id+"F0.imprint","IMPRINT",EDGE,{"derivedFrom":sQuery(id+"F0.wireOp",EDGE,"E0")}),-1.0]])]});
            extrude(context, id + "F1", {"entities" : qUnion([Q0]), "depth" : 3 * mm});
        }
        {
            var Q0;
            Q0=makeQuery(id+"F0.imprint","IMPRINT",FACE,{"disambiguationData":[TD([[makeQuery(id+"F0.imprint","IMPRINT",EDGE,{"derivedFrom":sQuery(id+"F0.wireOp",EDGE,"E322")}),-1.0]])]});
            extrude(context, id + "F2", {"entities" : qUnion([Q0]), "depth" : 3 * mm});
        }
        {
            var Q0;
            Q0=makeQuery(id+"F2.opExtrude","SWEPT_BODY",BODY,{"disambiguationData":[OSD([sQuery(id+"F0.wireOp",EDGE,"E322"),sQuery(id+"F0.wireOp",EDGE,"E323"),sQuery(id+"F0.wireOp",EDGE,"E324"),sQuery(id+"F0.wireOp",EDGE,"E325"),sQuery(id+"F0.wireOp",EDGE,"E326"),sQuery(id+"F0.wireOp",EDGE,"E327"),sQuery(id+"F0.wireOp",EDGE,"E328"),sQuery(id+"F0.wireOp",EDGE,"E329"),sQuery(id+"F0.wireOp",EDGE,"E330"),sQuery(id+"F0.wireOp",EDGE,"E331"),sQuery(id+"F0.wireOp",EDGE,"E332"),sQuery(id+"F0.wireOp",EDGE,"E333"),sQuery(id+"F0.wireOp",EDGE,"E334"),sQuery(id+"F0.wireOp",EDGE,"E335"),sQuery(id+"F0.wireOp",EDGE,"E336"),sQuery(id+"F0.wireOp",EDGE,"E337"),sQuery(id+"F0.wireOp",EDGE,"E338"),sQuery(id+"F0.wireOp",EDGE,"E339"),sQuery(id+"F0.wireOp",EDGE,"E340"),sQuery(id+"F0.wireOp",EDGE,"E341"),sQuery(id+"F0.wireOp",EDGE,"E342"),sQuery(id+"F0.wireOp",EDGE,"E343"),sQuery(id+"F0.wireOp",EDGE,"E344"),sQuery(id+"F0.wireOp",EDGE,"E345"),sQuery(id+"F0.wireOp",EDGE,"E346"),sQuery(id+"F0.wireOp",EDGE,"E347"),sQuery(id+"F0.wireOp",EDGE,"E348"),sQuery(id+"F0.wireOp",EDGE,"E349"),sQuery(id+"F0.wireOp",EDGE,"E350"),sQuery(id+"F0.wireOp",EDGE,"E351"),sQuery(id+"F0.wireOp",EDGE,"E352"),sQuery(id+"F0.wireOp",EDGE,"E353"),sQuery(id+"F0.wireOp",EDGE,"E354"),sQuery(id+"F0.wireOp",EDGE,"E355"),sQuery(id+"F0.wireOp",EDGE,"E356"),sQuery(id+"F0.wireOp",EDGE,"E357"),sQuery(id+"F0.wireOp",EDGE,"E358"),sQuery(id+"F0.wireOp",EDGE,"E359"),sQuery(id+"F0.wireOp",EDGE,"E360"),sQuery(id+"F0.wireOp",EDGE,"E361"),sQuery(id+"F0.wireOp",EDGE,"E362"),sQuery(id+"F0.wireOp",EDGE,"E363"),sQuery(id+"F0.wireOp",EDGE,"E364"),sQuery(id+"F0.wireOp",EDGE,"E365"),sQuery(id+"F0.wireOp",EDGE,"E366"),sQuery(id+"F0.wireOp",EDGE,"E367"),sQuery(id+"F0.wireOp",EDGE,"E368"),sQuery(id+"F0.wireOp",EDGE,"E369"),sQuery(id+"F0.wireOp",EDGE,"E370"),sQuery(id+"F0.wireOp",EDGE,"E371"),sQuery(id+"F0.wireOp",EDGE,"E372"),sQuery(id+"F0.wireOp",EDGE,"E373"),sQuery(id+"F0.wireOp",EDGE,"E374"),sQuery(id+"F0.wireOp",EDGE,"E375"),sQuery(id+"F0.wireOp",EDGE,"E376"),sQuery(id+"F0.wireOp",EDGE,"E377"),sQuery(id+"F0.wireOp",EDGE,"E378"),sQuery(id+"F0.wireOp",EDGE,"E379"),sQuery(id+"F0.wireOp",EDGE,"E380"),sQuery(id+"F0.wireOp",EDGE,"E381"),sQuery(id+"F0.wireOp",EDGE,"E382"),sQuery(id+"F0.wireOp",EDGE,"E383"),sQuery(id+"F0.wireOp",EDGE,"E384"),sQuery(id+"F0.wireOp",EDGE,"E385"),sQuery(id+"F0.wireOp",EDGE,"E386"),sQuery(id+"F0.wireOp",EDGE,"E387"),sQuery(id+"F0.wireOp",EDGE,"E388"),sQuery(id+"F0.wireOp",EDGE,"E389"),sQuery(id+"F0.wireOp",EDGE,"E390"),sQuery(id+"F0.wireOp",EDGE,"E391"),sQuery(id+"F0.wireOp",EDGE,"E392"),sQuery(id+"F0.wireOp",EDGE,"E393"),sQuery(id+"F0.wireOp",EDGE,"E394"),sQuery(id+"F0.wireOp",EDGE,"E395"),sQuery(id+"F0.wireOp",EDGE,"E396"),sQuery(id+"F0.wireOp",EDGE,"E397"),sQuery(id+"F0.wireOp",EDGE,"E398"),sQuery(id+"F0.wireOp",EDGE,"E399"),sQuery(id+"F0.wireOp",EDGE,"E400"),sQuery(id+"F0.wireOp",EDGE,"E401"),sQuery(id+"F0.wireOp",EDGE,"E402"),sQuery(id+"F0.wireOp",EDGE,"E403"),sQuery(id+"F0.wireOp",EDGE,"E404"),sQuery(id+"F0.wireOp",EDGE,"E405"),sQuery(id+"F0.wireOp",EDGE,"E406"),sQuery(id+"F0.wireOp",EDGE,"E407"),sQuery(id+"F0.wireOp",EDGE,"E408"),sQuery(id+"F0.wireOp",EDGE,"E409"),sQuery(id+"F0.wireOp",EDGE,"E410"),sQuery(id+"F0.wireOp",EDGE,"E411"),sQuery(id+"F0.wireOp",EDGE,"E412"),sQuery(id+"F0.wireOp",EDGE,"E413"),sQuery(id+"F0.wireOp",EDGE,"E414"),sQuery(id+"F0.wireOp",EDGE,"E415"),sQuery(id+"F0.wireOp",EDGE,"E416"),sQuery(id+"F0.wireOp",EDGE,"E417"),sQuery(id+"F0.wireOp",EDGE,"E418"),sQuery(id+"F0.wireOp",EDGE,"E419"),sQuery(id+"F0.wireOp",EDGE,"E420"),sQuery(id+"F0.wireOp",EDGE,"E421"),sQuery(id+"F0.wireOp",EDGE,"E422"),sQuery(id+"F0.wireOp",EDGE,"E423"),sQuery(id+"F0.wireOp",EDGE,"E424"),sQuery(id+"F0.wireOp",EDGE,"E425"),sQuery(id+"F0.wireOp",EDGE,"E426"),sQuery(id+"F0.wireOp",EDGE,"E427"),sQuery(id+"F0.wireOp",EDGE,"E428"),sQuery(id+"F0.wireOp",EDGE,"E429"),sQuery(id+"F0.wireOp",EDGE,"E430"),sQuery(id+"F0.wireOp",EDGE,"E431"),sQuery(id+"F0.wireOp",EDGE,"E432"),sQuery(id+"F0.wireOp",EDGE,"E433"),sQuery(id+"F0.wireOp",EDGE,"E434"),sQuery(id+"F0.wireOp",EDGE,"E435"),sQuery(id+"F0.wireOp",EDGE,"E436"),sQuery(id+"F0.wireOp",EDGE,"E437"),sQuery(id+"F0.wireOp",EDGE,"E438"),sQuery(id+"F0.wireOp",EDGE,"E439"),sQuery(id+"F0.wireOp",EDGE,"E440"),sQuery(id+"F0.wireOp",EDGE,"E441"),sQuery(id+"F0.wireOp",EDGE,"E442"),sQuery(id+"F0.wireOp",EDGE,"E443"),sQuery(id+"F0.wireOp",EDGE,"E444"),sQuery(id+"F0.wireOp",EDGE,"E445"),sQuery(id+"F0.wireOp",EDGE,"E446"),sQuery(id+"F0.wireOp",EDGE,"E447"),sQuery(id+"F0.wireOp",EDGE,"E448"),sQuery(id+"F0.wireOp",EDGE,"E449"),sQuery(id+"F0.wireOp",EDGE,"E450"),sQuery(id+"F0.wireOp",EDGE,"E451"),sQuery(id+"F0.wireOp",EDGE,"E452"),sQuery(id+"F0.wireOp",EDGE,"E453"),sQuery(id+"F0.wireOp",EDGE,"E454"),sQuery(id+"F0.wireOp",EDGE,"E455"),sQuery(id+"F0.wireOp",EDGE,"E456"),sQuery(id+"F0.wireOp",EDGE,"E457"),sQuery(id+"F0.wireOp",EDGE,"E458"),sQuery(id+"F0.wireOp",EDGE,"E459"),sQuery(id+"F0.wireOp",EDGE,"E460"),sQuery(id+"F0.wireOp",EDGE,"E461"),sQuery(id+"F0.wireOp",EDGE,"E462"),sQuery(id+"F0.wireOp",EDGE,"E463"),sQuery(id+"F0.wireOp",EDGE,"E464"),sQuery(id+"F0.wireOp",EDGE,"E465"),sQuery(id+"F0.wireOp",EDGE,"E471"),sQuery(id+"F0.wireOp",EDGE,"E477"),sQuery(id+"F0.wireOp",EDGE,"E469"),sQuery(id+"F0.wireOp",EDGE,"E479"),sQuery(id+"F0.wireOp",EDGE,"E475"),sQuery(id+"F0.wireOp",EDGE,"E481"),sQuery(id+"F0.wireOp",EDGE,"E466"),sQuery(id+"F0.wireOp",EDGE,"E484"),sQuery(id+"F0.wireOp",EDGE,"E483"),sQuery(id+"F0.wireOp",EDGE,"E482"),sQuery(id+"F0.wireOp",EDGE,"E480"),sQuery(id+"F0.wireOp",EDGE,"E478"),sQuery(id+"F0.wireOp",EDGE,"E476"),sQuery(id+"F0.wireOp",EDGE,"E474"),sQuery(id+"F0.wireOp",EDGE,"E473"),sQuery(id+"F0.wireOp",EDGE,"E472"),sQuery(id+"F0.wireOp",EDGE,"E470"),sQuery(id+"F0.wireOp",EDGE,"E468"),sQuery(id+"F0.wireOp",EDGE,"E467")])]});
            transform(context, id + "F3", {"entities" : qUnion([Q0]), "transformType" : TransformType.TRANSLATION_3D, "dx" : 0 * mm, "dy" : 0 * mm, "dz" : 22 * mm, "makeCopy" : false});
        }
        {
            var Q0;
            Q0=makeQuery(id+"F1.opExtrude","SWEPT_BODY",BODY,{"disambiguationData":[OSD([sQuery(id+"F0.wireOp",EDGE,"E0"),sQuery(id+"F0.wireOp",EDGE,"E1"),sQuery(id+"F0.wireOp",EDGE,"E2"),sQuery(id+"F0.wireOp",EDGE,"E3"),sQuery(id+"F0.wireOp",EDGE,"E4"),sQuery(id+"F0.wireOp",EDGE,"E5"),sQuery(id+"F0.wireOp",EDGE,"E6"),sQuery(id+"F0.wireOp",EDGE,"E7"),sQuery(id+"F0.wireOp",EDGE,"E8"),sQuery(id+"F0.wireOp",EDGE,"E9"),sQuery(id+"F0.wireOp",EDGE,"E10"),sQuery(id+"F0.wireOp",EDGE,"E11"),sQuery(id+"F0.wireOp",EDGE,"E12"),sQuery(id+"F0.wireOp",EDGE,"E13"),sQuery(id+"F0.wireOp",EDGE,"E14"),sQuery(id+"F0.wireOp",EDGE,"E15"),sQuery(id+"F0.wireOp",EDGE,"E16"),sQuery(id+"F0.wireOp",EDGE,"E17"),sQuery(id+"F0.wireOp",EDGE,"E18"),sQuery(id+"F0.wireOp",EDGE,"E19"),sQuery(id+"F0.wireOp",EDGE,"E20"),sQuery(id+"F0.wireOp",EDGE,"E21"),sQuery(id+"F0.wireOp",EDGE,"E22"),sQuery(id+"F0.wireOp",EDGE,"E23"),sQuery(id+"F0.wireOp",EDGE,"E24"),sQuery(id+"F0.wireOp",EDGE,"E25"),sQuery(id+"F0.wireOp",EDGE,"E26"),sQuery(id+"F0.wireOp",EDGE,"E27"),sQuery(id+"F0.wireOp",EDGE,"E28"),sQuery(id+"F0.wireOp",EDGE,"E29"),sQuery(id+"F0.wireOp",EDGE,"E30"),sQuery(id+"F0.wireOp",EDGE,"E31"),sQuery(id+"F0.wireOp",EDGE,"E32"),sQuery(id+"F0.wireOp",EDGE,"E33"),sQuery(id+"F0.wireOp",EDGE,"E34"),sQuery(id+"F0.wireOp",EDGE,"E35"),sQuery(id+"F0.wireOp",EDGE,"E36"),sQuery(id+"F0.wireOp",EDGE,"E37"),sQuery(id+"F0.wireOp",EDGE,"E38"),sQuery(id+"F0.wireOp",EDGE,"E39"),sQuery(id+"F0.wireOp",EDGE,"E40"),sQuery(id+"F0.wireOp",EDGE,"E41"),sQuery(id+"F0.wireOp",EDGE,"E42"),sQuery(id+"F0.wireOp",EDGE,"E43"),sQuery(id+"F0.wireOp",EDGE,"E44"),sQuery(id+"F0.wireOp",EDGE,"E45"),sQuery(id+"F0.wireOp",EDGE,"E46"),sQuery(id+"F0.wireOp",EDGE,"E47"),sQuery(id+"F0.wireOp",EDGE,"E48"),sQuery(id+"F0.wireOp",EDGE,"E49"),sQuery(id+"F0.wireOp",EDGE,"E50"),sQuery(id+"F0.wireOp",EDGE,"E51"),sQuery(id+"F0.wireOp",EDGE,"E52"),sQuery(id+"F0.wireOp",EDGE,"E53"),sQuery(id+"F0.wireOp",EDGE,"E54"),sQuery(id+"F0.wireOp",EDGE,"E55"),sQuery(id+"F0.wireOp",EDGE,"E56"),sQuery(id+"F0.wireOp",EDGE,"E57"),sQuery(id+"F0.wireOp",EDGE,"E58"),sQuery(id+"F0.wireOp",EDGE,"E59"),sQuery(id+"F0.wireOp",EDGE,"E60"),sQuery(id+"F0.wireOp",EDGE,"E61"),sQuery(id+"F0.wireOp",EDGE,"E62"),sQuery(id+"F0.wireOp",EDGE,"E63"),sQuery(id+"F0.wireOp",EDGE,"E64"),sQuery(id+"F0.wireOp",EDGE,"E65"),sQuery(id+"F0.wireOp",EDGE,"E66"),sQuery(id+"F0.wireOp",EDGE,"E67"),sQuery(id+"F0.wireOp",EDGE,"E68"),sQuery(id+"F0.wireOp",EDGE,"E69"),sQuery(id+"F0.wireOp",EDGE,"E70"),sQuery(id+"F0.wireOp",EDGE,"E71"),sQuery(id+"F0.wireOp",EDGE,"E72"),sQuery(id+"F0.wireOp",EDGE,"E73"),sQuery(id+"F0.wireOp",EDGE,"E74"),sQuery(id+"F0.wireOp",EDGE,"E75"),sQuery(id+"F0.wireOp",EDGE,"E76"),sQuery(id+"F0.wireOp",EDGE,"E77"),sQuery(id+"F0.wireOp",EDGE,"E78"),sQuery(id+"F0.wireOp",EDGE,"E79"),sQuery(id+"F0.wireOp",EDGE,"E80"),sQuery(id+"F0.wireOp",EDGE,"E81"),sQuery(id+"F0.wireOp",EDGE,"E82"),sQuery(id+"F0.wireOp",EDGE,"E83"),sQuery(id+"F0.wireOp",EDGE,"E84"),sQuery(id+"F0.wireOp",EDGE,"E85"),sQuery(id+"F0.wireOp",EDGE,"E86"),sQuery(id+"F0.wireOp",EDGE,"E87"),sQuery(id+"F0.wireOp",EDGE,"E88"),sQuery(id+"F0.wireOp",EDGE,"E89"),sQuery(id+"F0.wireOp",EDGE,"E90"),sQuery(id+"F0.wireOp",EDGE,"E91"),sQuery(id+"F0.wireOp",EDGE,"E92"),sQuery(id+"F0.wireOp",EDGE,"E93"),sQuery(id+"F0.wireOp",EDGE,"E94"),sQuery(id+"F0.wireOp",EDGE,"E95"),sQuery(id+"F0.wireOp",EDGE,"E96"),sQuery(id+"F0.wireOp",EDGE,"E97"),sQuery(id+"F0.wireOp",EDGE,"E98"),sQuery(id+"F0.wireOp",EDGE,"E99"),sQuery(id+"F0.wireOp",EDGE,"E100"),sQuery(id+"F0.wireOp",EDGE,"E101"),sQuery(id+"F0.wireOp",EDGE,"E102"),sQuery(id+"F0.wireOp",EDGE,"E103"),sQuery(id+"F0.wireOp",EDGE,"E104"),sQuery(id+"F0.wireOp",EDGE,"E105"),sQuery(id+"F0.wireOp",EDGE,"E106"),sQuery(id+"F0.wireOp",EDGE,"E107"),sQuery(id+"F0.wireOp",EDGE,"E108"),sQuery(id+"F0.wireOp",EDGE,"E109"),sQuery(id+"F0.wireOp",EDGE,"E110"),sQuery(id+"F0.wireOp",EDGE,"E111"),sQuery(id+"F0.wireOp",EDGE,"E112"),sQuery(id+"F0.wireOp",EDGE,"E113"),sQuery(id+"F0.wireOp",EDGE,"E114"),sQuery(id+"F0.wireOp",EDGE,"E115"),sQuery(id+"F0.wireOp",EDGE,"E116"),sQuery(id+"F0.wireOp",EDGE,"E117"),sQuery(id+"F0.wireOp",EDGE,"E118"),sQuery(id+"F0.wireOp",EDGE,"E119"),sQuery(id+"F0.wireOp",EDGE,"E120"),sQuery(id+"F0.wireOp",EDGE,"E121"),sQuery(id+"F0.wireOp",EDGE,"E122"),sQuery(id+"F0.wireOp",EDGE,"E123"),sQuery(id+"F0.wireOp",EDGE,"E124"),sQuery(id+"F0.wireOp",EDGE,"E125"),sQuery(id+"F0.wireOp",EDGE,"E126"),sQuery(id+"F0.wireOp",EDGE,"E127"),sQuery(id+"F0.wireOp",EDGE,"E128"),sQuery(id+"F0.wireOp",EDGE,"E129"),sQuery(id+"F0.wireOp",EDGE,"E130"),sQuery(id+"F0.wireOp",EDGE,"E131"),sQuery(id+"F0.wireOp",EDGE,"E132"),sQuery(id+"F0.wireOp",EDGE,"E133"),sQuery(id+"F0.wireOp",EDGE,"E134"),sQuery(id+"F0.wireOp",EDGE,"E135"),sQuery(id+"F0.wireOp",EDGE,"E136"),sQuery(id+"F0.wireOp",EDGE,"E137"),sQuery(id+"F0.wireOp",EDGE,"E138"),sQuery(id+"F0.wireOp",EDGE,"E139"),sQuery(id+"F0.wireOp",EDGE,"E140"),sQuery(id+"F0.wireOp",EDGE,"E141"),sQuery(id+"F0.wireOp",EDGE,"E142"),sQuery(id+"F0.wireOp",EDGE,"E143"),sQuery(id+"F0.wireOp",EDGE,"E144"),sQuery(id+"F0.wireOp",EDGE,"E145"),sQuery(id+"F0.wireOp",EDGE,"E146"),sQuery(id+"F0.wireOp",EDGE,"E147"),sQuery(id+"F0.wireOp",EDGE,"E148"),sQuery(id+"F0.wireOp",EDGE,"E149"),sQuery(id+"F0.wireOp",EDGE,"E150"),sQuery(id+"F0.wireOp",EDGE,"E151"),sQuery(id+"F0.wireOp",EDGE,"E152"),sQuery(id+"F0.wireOp",EDGE,"E153"),sQuery(id+"F0.wireOp",EDGE,"E154"),sQuery(id+"F0.wireOp",EDGE,"E155"),sQuery(id+"F0.wireOp",EDGE,"E156"),sQuery(id+"F0.wireOp",EDGE,"E157"),sQuery(id+"F0.wireOp",EDGE,"E158"),sQuery(id+"F0.wireOp",EDGE,"E159"),sQuery(id+"F0.wireOp",EDGE,"E160"),sQuery(id+"F0.wireOp",EDGE,"E161"),sQuery(id+"F0.wireOp",EDGE,"E162"),sQuery(id+"F0.wireOp",EDGE,"E163"),sQuery(id+"F0.wireOp",EDGE,"E164"),sQuery(id+"F0.wireOp",EDGE,"E165"),sQuery(id+"F0.wireOp",EDGE,"E166"),sQuery(id+"F0.wireOp",EDGE,"E167"),sQuery(id+"F0.wireOp",EDGE,"E168"),sQuery(id+"F0.wireOp",EDGE,"E169"),sQuery(id+"F0.wireOp",EDGE,"E170"),sQuery(id+"F0.wireOp",EDGE,"E171"),sQuery(id+"F0.wireOp",EDGE,"E172"),sQuery(id+"F0.wireOp",EDGE,"E173"),sQuery(id+"F0.wireOp",EDGE,"E174"),sQuery(id+"F0.wireOp",EDGE,"E175"),sQuery(id+"F0.wireOp",EDGE,"E176"),sQuery(id+"F0.wireOp",EDGE,"E177"),sQuery(id+"F0.wireOp",EDGE,"E178"),sQuery(id+"F0.wireOp",EDGE,"E179"),sQuery(id+"F0.wireOp",EDGE,"E180"),sQuery(id+"F0.wireOp",EDGE,"E181"),sQuery(id+"F0.wireOp",EDGE,"E182"),sQuery(id+"F0.wireOp",EDGE,"E183"),sQuery(id+"F0.wireOp",EDGE,"E184"),sQuery(id+"F0.wireOp",EDGE,"E185"),sQuery(id+"F0.wireOp",EDGE,"E186"),sQuery(id+"F0.wireOp",EDGE,"E187"),sQuery(id+"F0.wireOp",EDGE,"E188"),sQuery(id+"F0.wireOp",EDGE,"E189"),sQuery(id+"F0.wireOp",EDGE,"E190"),sQuery(id+"F0.wireOp",EDGE,"E191"),sQuery(id+"F0.wireOp",EDGE,"E192"),sQuery(id+"F0.wireOp",EDGE,"E193"),sQuery(id+"F0.wireOp",EDGE,"E194"),sQuery(id+"F0.wireOp",EDGE,"E195"),sQuery(id+"F0.wireOp",EDGE,"E196"),sQuery(id+"F0.wireOp",EDGE,"E197"),sQuery(id+"F0.wireOp",EDGE,"E198"),sQuery(id+"F0.wireOp",EDGE,"E199"),sQuery(id+"F0.wireOp",EDGE,"E200"),sQuery(id+"F0.wireOp",EDGE,"E201"),sQuery(id+"F0.wireOp",EDGE,"E202"),sQuery(id+"F0.wireOp",EDGE,"E203"),sQuery(id+"F0.wireOp",EDGE,"E204"),sQuery(id+"F0.wireOp",EDGE,"E205"),sQuery(id+"F0.wireOp",EDGE,"E206"),sQuery(id+"F0.wireOp",EDGE,"E207"),sQuery(id+"F0.wireOp",EDGE,"E208"),sQuery(id+"F0.wireOp",EDGE,"E209"),sQuery(id+"F0.wireOp",EDGE,"E210"),sQuery(id+"F0.wireOp",EDGE,"E211"),sQuery(id+"F0.wireOp",EDGE,"E212"),sQuery(id+"F0.wireOp",EDGE,"E213"),sQuery(id+"F0.wireOp",EDGE,"E214"),sQuery(id+"F0.wireOp",EDGE,"E215"),sQuery(id+"F0.wireOp",EDGE,"E216"),sQuery(id+"F0.wireOp",EDGE,"E217"),sQuery(id+"F0.wireOp",EDGE,"E218"),sQuery(id+"F0.wireOp",EDGE,"E219"),sQuery(id+"F0.wireOp",EDGE,"E220"),sQuery(id+"F0.wireOp",EDGE,"E221"),sQuery(id+"F0.wireOp",EDGE,"E222"),sQuery(id+"F0.wireOp",EDGE,"E223"),sQuery(id+"F0.wireOp",EDGE,"E224"),sQuery(id+"F0.wireOp",EDGE,"E225"),sQuery(id+"F0.wireOp",EDGE,"E226"),sQuery(id+"F0.wireOp",EDGE,"E227"),sQuery(id+"F0.wireOp",EDGE,"E228"),sQuery(id+"F0.wireOp",EDGE,"E229"),sQuery(id+"F0.wireOp",EDGE,"E230"),sQuery(id+"F0.wireOp",EDGE,"E231"),sQuery(id+"F0.wireOp",EDGE,"E232"),sQuery(id+"F0.wireOp",EDGE,"E233"),sQuery(id+"F0.wireOp",EDGE,"E234"),sQuery(id+"F0.wireOp",EDGE,"E235"),sQuery(id+"F0.wireOp",EDGE,"E236"),sQuery(id+"F0.wireOp",EDGE,"E237"),sQuery(id+"F0.wireOp",EDGE,"E238"),sQuery(id+"F0.wireOp",EDGE,"E239"),sQuery(id+"F0.wireOp",EDGE,"E240"),sQuery(id+"F0.wireOp",EDGE,"E241"),sQuery(id+"F0.wireOp",EDGE,"E242"),sQuery(id+"F0.wireOp",EDGE,"E243"),sQuery(id+"F0.wireOp",EDGE,"E244"),sQuery(id+"F0.wireOp",EDGE,"E245"),sQuery(id+"F0.wireOp",EDGE,"E246"),sQuery(id+"F0.wireOp",EDGE,"E247"),sQuery(id+"F0.wireOp",EDGE,"E248"),sQuery(id+"F0.wireOp",EDGE,"E249"),sQuery(id+"F0.wireOp",EDGE,"E250"),sQuery(id+"F0.wireOp",EDGE,"E251"),sQuery(id+"F0.wireOp",EDGE,"E252"),sQuery(id+"F0.wireOp",EDGE,"E253"),sQuery(id+"F0.wireOp",EDGE,"E254"),sQuery(id+"F0.wireOp",EDGE,"E255"),sQuery(id+"F0.wireOp",EDGE,"E256"),sQuery(id+"F0.wireOp",EDGE,"E257"),sQuery(id+"F0.wireOp",EDGE,"E258"),sQuery(id+"F0.wireOp",EDGE,"E259"),sQuery(id+"F0.wireOp",EDGE,"E260"),sQuery(id+"F0.wireOp",EDGE,"E261"),sQuery(id+"F0.wireOp",EDGE,"E262"),sQuery(id+"F0.wireOp",EDGE,"E263"),sQuery(id+"F0.wireOp",EDGE,"E264"),sQuery(id+"F0.wireOp",EDGE,"E265"),sQuery(id+"F0.wireOp",EDGE,"E266"),sQuery(id+"F0.wireOp",EDGE,"E267"),sQuery(id+"F0.wireOp",EDGE,"E268"),sQuery(id+"F0.wireOp",EDGE,"E269"),sQuery(id+"F0.wireOp",EDGE,"E270"),sQuery(id+"F0.wireOp",EDGE,"E271"),sQuery(id+"F0.wireOp",EDGE,"E272"),sQuery(id+"F0.wireOp",EDGE,"E273"),sQuery(id+"F0.wireOp",EDGE,"E274"),sQuery(id+"F0.wireOp",EDGE,"E275"),sQuery(id+"F0.wireOp",EDGE,"E276"),sQuery(id+"F0.wireOp",EDGE,"E277"),sQuery(id+"F0.wireOp",EDGE,"E278"),sQuery(id+"F0.wireOp",EDGE,"E279"),sQuery(id+"F0.wireOp",EDGE,"E280"),sQuery(id+"F0.wireOp",EDGE,"E281"),sQuery(id+"F0.wireOp",EDGE,"E282"),sQuery(id+"F0.wireOp",EDGE,"E283"),sQuery(id+"F0.wireOp",EDGE,"E284"),sQuery(id+"F0.wireOp",EDGE,"E285"),sQuery(id+"F0.wireOp",EDGE,"E286"),sQuery(id+"F0.wireOp",EDGE,"E287"),sQuery(id+"F0.wireOp",EDGE,"E288"),sQuery(id+"F0.wireOp",EDGE,"E289"),sQuery(id+"F0.wireOp",EDGE,"E290"),sQuery(id+"F0.wireOp",EDGE,"E291"),sQuery(id+"F0.wireOp",EDGE,"E292"),sQuery(id+"F0.wireOp",EDGE,"E293"),sQuery(id+"F0.wireOp",EDGE,"E294"),sQuery(id+"F0.wireOp",EDGE,"E295"),sQuery(id+"F0.wireOp",EDGE,"E296"),sQuery(id+"F0.wireOp",EDGE,"E297"),sQuery(id+"F0.wireOp",EDGE,"E298"),sQuery(id+"F0.wireOp",EDGE,"E299"),sQuery(id+"F0.wireOp",EDGE,"E300"),sQuery(id+"F0.wireOp",EDGE,"E301"),sQuery(id+"F0.wireOp",EDGE,"E302"),sQuery(id+"F0.wireOp",EDGE,"E303"),sQuery(id+"F0.wireOp",EDGE,"E304"),sQuery(id+"F0.wireOp",EDGE,"E305"),sQuery(id+"F0.wireOp",EDGE,"E306"),sQuery(id+"F0.wireOp",EDGE,"E307"),sQuery(id+"F0.wireOp",EDGE,"E308"),sQuery(id+"F0.wireOp",EDGE,"E309"),sQuery(id+"F0.wireOp",EDGE,"E310"),sQuery(id+"F0.wireOp",EDGE,"E311"),sQuery(id+"F0.wireOp",EDGE,"E312"),sQuery(id+"F0.wireOp",EDGE,"E313"),sQuery(id+"F0.wireOp",EDGE,"E314"),sQuery(id+"F0.wireOp",EDGE,"E315"),sQuery(id+"F0.wireOp",EDGE,"E316"),sQuery(id+"F0.wireOp",EDGE,"E317"),sQuery(id+"F0.wireOp",EDGE,"E318"),sQuery(id+"F0.wireOp",EDGE,"E319"),sQuery(id+"F0.wireOp",EDGE,"E320"),sQuery(id+"F0.wireOp",EDGE,"E321")])]});
            var Q1;
            Q1=makeQuery(id+"F1.opExtrude","SWEPT_EDGE",EDGE,{"disambiguationData":[OSD([sQuery(id+"F0.wireOp",EDGE,"E44"),sQuery(id+"F0.wireOp",EDGE,"E45")])]});
            transform(context, id + "F4", {"entities" : qUnion([Q0]), "transformType" : TransformType.ROTATION, "transformAxis" : qUnion([Q1]), "angle" : 90 * degree, "makeCopy" : false});
        }
    });
